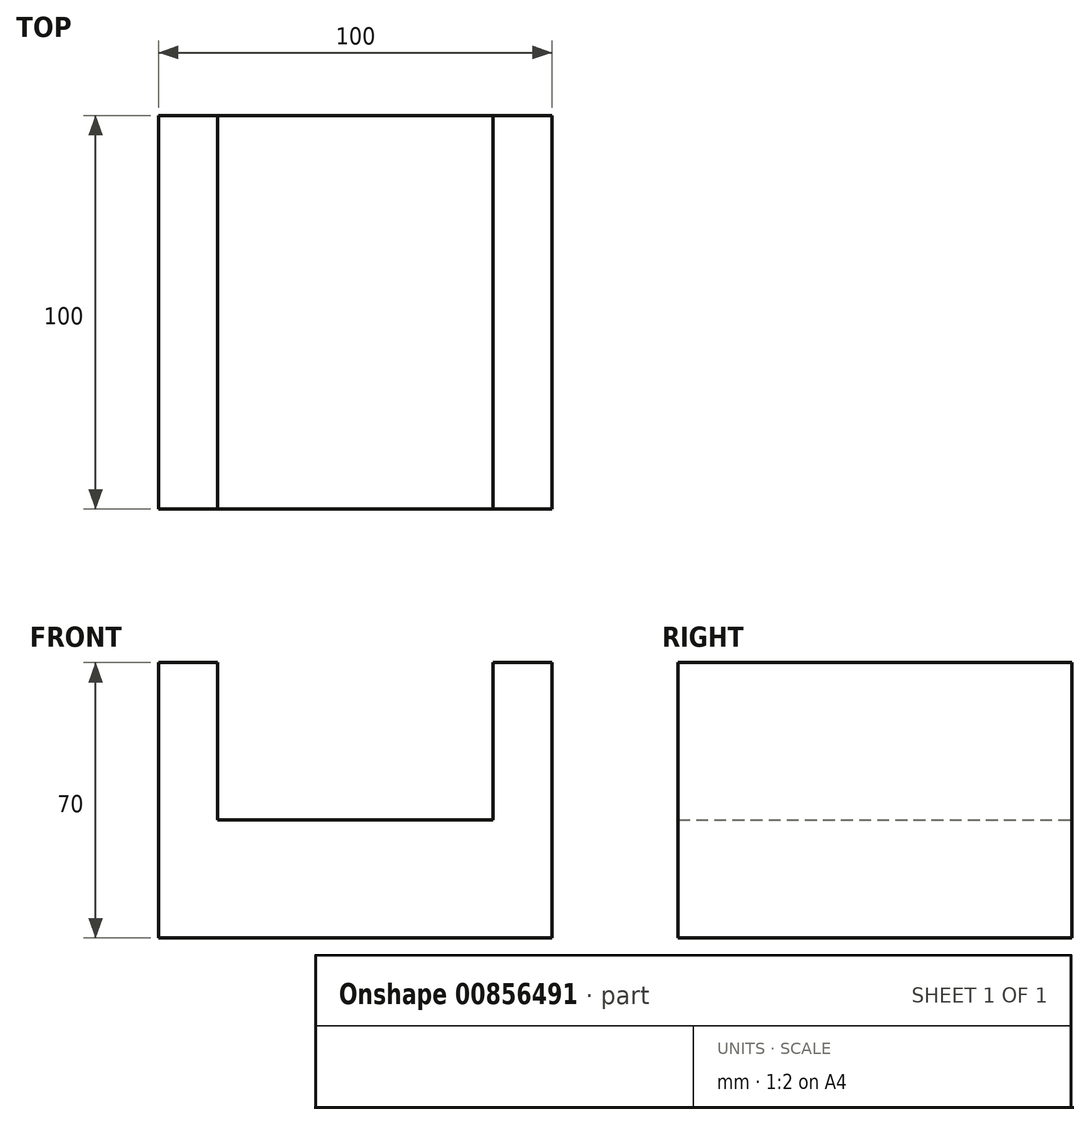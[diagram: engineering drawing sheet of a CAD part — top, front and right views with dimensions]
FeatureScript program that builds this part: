
annotation { "Feature Type Name" : "Feature", "Feature Type Description" : "" }
export const myFeature = defineFeature(function(context is Context, id is Id, definition is map)
    precondition{}
    {
        {
            var Q0;
            Q0=qCreatedBy(makeId("Front.planeOp"),FACE);
            var sketch = newSketch(context, id + "F0", { "sketchPlane" : qUnion([Q0])});
            skLineSegment(sketch, "E0.bottom", {"start": v(-50, 12.26) * mm, "end": v(50, 12.26) * mm});
            skLineSegment(sketch, "E0.top", {"start": v(-50, -17.74) * mm, "end": v(50, -17.74) * mm});
            skLineSegment(sketch, "E0.left", {"start": v(-50, 12.26) * mm, "end": v(-50, -17.74) * mm});
            skLineSegment(sketch, "E0.right", {"start": v(50, 12.26) * mm, "end": v(50, -17.74) * mm});
            skPoint(sketch, "E0.middle", {"position": v(0, -2.74) * mm});
            skLineSegment(sketch, "E1.bottom", {"start": v(-50, 12.26) * mm, "end": v(-35, 12.26) * mm});
            skLineSegment(sketch, "E1.top", {"start": v(-50, 52.26) * mm, "end": v(-35, 52.26) * mm});
            skLineSegment(sketch, "E1.left", {"start": v(-50, 12.26) * mm, "end": v(-50, 52.26) * mm});
            skLineSegment(sketch, "E1.right", {"start": v(-35, 12.26) * mm, "end": v(-35, 52.26) * mm});
            skLineSegment(sketch, "E2.bottom", {"start": v(50, 12.26) * mm, "end": v(35, 12.26) * mm});
            skLineSegment(sketch, "E2.top", {"start": v(50, 52.26) * mm, "end": v(35, 52.26) * mm});
            skLineSegment(sketch, "E2.left", {"start": v(50, 12.26) * mm, "end": v(50, 52.26) * mm});
            skLineSegment(sketch, "E2.right", {"start": v(35, 12.26) * mm, "end": v(35, 52.26) * mm});
            skSolve(sketch);
        }
        {
            var Q0;
            Q0 = qSketchRegion(id + "F0", true);
            extrude(context, id + "F1", {"entities" : qUnion([Q0]), "endBound" : BoundingType.SYMMETRIC, "depth" : 100 * mm, "offsetDistance" : 25.4 * mm});
        }
    });
